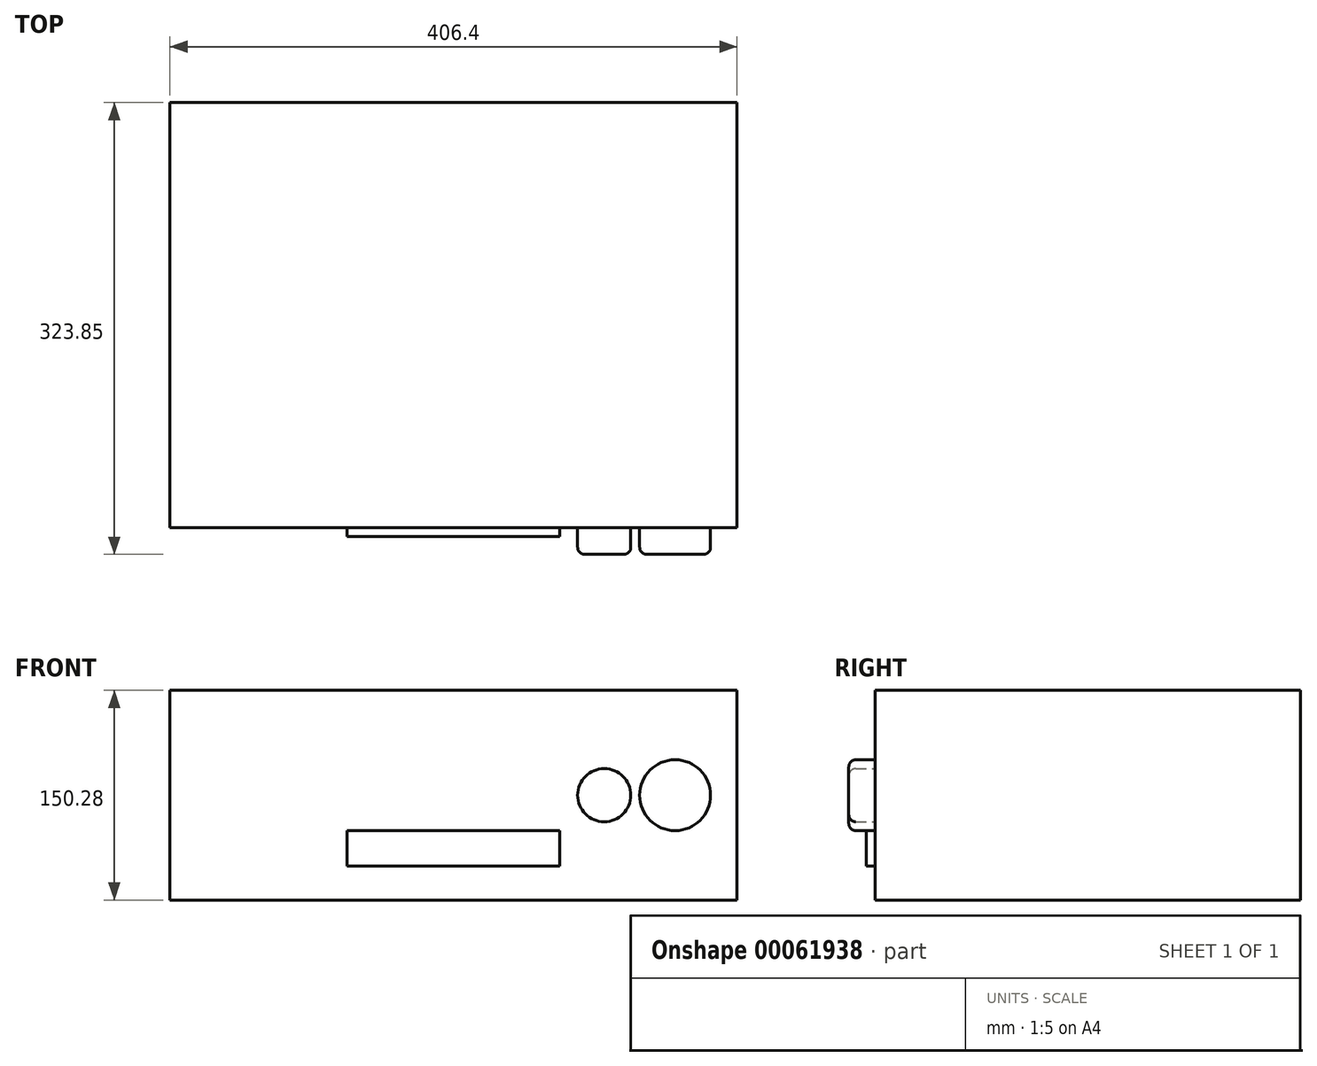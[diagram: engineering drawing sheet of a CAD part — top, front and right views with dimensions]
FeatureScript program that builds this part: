
annotation { "Feature Type Name" : "Feature", "Feature Type Description" : "" }
export const myFeature = defineFeature(function(context is Context, id is Id, definition is map)
    precondition{}
    {
        {
            var Q0;
            Q0=qCreatedBy(makeId("Front.planeOp"),FACE);
            var sketch = newSketch(context, id + "F0", { "sketchPlane" : qUnion([Q0])});
            skLineSegment(sketch, "E0.rect.bottom", {"start": v(203.2, -75.14) * mm, "end": v(-203.2, -75.14) * mm});
            skLineSegment(sketch, "E0.rect.top", {"start": v(203.2, 75.14) * mm, "end": v(-203.2, 75.14) * mm});
            skLineSegment(sketch, "E0.rect.left", {"start": v(203.2, -75.14) * mm, "end": v(203.2, 75.14) * mm});
            skLineSegment(sketch, "E0.rect.right", {"start": v(-203.2, -75.14) * mm, "end": v(-203.2, 75.14) * mm});
            skPoint(sketch, "E0.rect.middle", {"position": v(0, 0) * mm});
            skSolve(sketch);
        }
        {
            var Q0;
            Q0=makeQuery(id+"F0.imprint","IMPRINT",FACE,{"disambiguationData":[TD([[makeQuery(id+"F0.imprint","IMPRINT",EDGE,{"derivedFrom":sQuery(id+"F0.wireOp",EDGE,"E0.rect.bottom")}),-1.0]])]});
            extrude(context, id + "F1", {"entities" : qUnion([Q0]), "oppositeDirection" : true, "depth" : 304.8 * mm});
        }
        {
            var Q0;
            Q0=makeQuery(id+"F1.opExtrude","CAP_FACE",FACE,{"disambiguationData":[OSD([sQuery(id+"F0.wireOp",EDGE,"E0.rect.bottom"),sQuery(id+"F0.wireOp",EDGE,"E0.rect.top"),sQuery(id+"F0.wireOp",EDGE,"E0.rect.left"),sQuery(id+"F0.wireOp",EDGE,"E0.rect.right")])],"isStart":true});
            var sketch = newSketch(context, id + "F2", { "sketchPlane" : qUnion([Q0])});
            skLineSegment(sketch, "E1", {"start": v(203.2, 0) * mm, "end": v(158.75, 0) * mm, "construction": true});
            skPoint(sketch, "E1.endSnap0", {"position": v(203.2, 0) * mm});
            skLineSegment(sketch, "E2", {"start": v(158.75, 0) * mm, "end": v(107.95, 0) * mm, "construction": true});
            skCircle(sketch, "E3", {"center": v(158.75, 0) * mm, "radius": 25.4 * mm});
            skCircle(sketch, "E4", {"center": v(107.95, 0) * mm, "radius": 19.05 * mm});
            skSolve(sketch);
        }
        {
            var Q0;
            Q0=makeQuery(id+"F2.imprint","IMPRINT",FACE,{"disambiguationData":[TD([[makeQuery(id+"F2.imprint","IMPRINT",EDGE,{"derivedFrom":sQuery(id+"F2.wireOp",EDGE,"E4")}),1.0]])]});
            var Q1;
            Q1=makeQuery(id+"F2.imprint","IMPRINT",FACE,{"disambiguationData":[TD([[makeQuery(id+"F2.imprint","IMPRINT",EDGE,{"derivedFrom":sQuery(id+"F2.wireOp",EDGE,"E3")}),1.0]])]});
            extrude(context, id + "F3", {"entities" : qUnion([Q0, Q1]), "depth" : 19.05 * mm});
        }
        {
            var Q0;
            Q0=makeQuery(id+"F3.opExtrude","CAP_EDGE",EDGE,{"disambiguationData":[OSD([sQuery(id+"F2.wireOp",EDGE,"E4")])],"isStart":false});
            var Q1;
            Q1=makeQuery(id+"F3.opExtrude","CAP_EDGE",EDGE,{"disambiguationData":[OSD([sQuery(id+"F2.wireOp",EDGE,"E3")])],"isStart":false});
            fillet(context, id + "F4", {"entities" : qUnion([Q0, Q1]), "radius" : 5.08 * mm, "tangentPropagation" : true, "allowEdgeOverflow" : false});
        }
        {
            var Q0;
            Q0=makeQuery(id+"F1.opExtrude","CAP_FACE",FACE,{"disambiguationData":[OSD([sQuery(id+"F0.wireOp",EDGE,"E0.rect.bottom"),sQuery(id+"F0.wireOp",EDGE,"E0.rect.top"),sQuery(id+"F0.wireOp",EDGE,"E0.rect.left"),sQuery(id+"F0.wireOp",EDGE,"E0.rect.right")])],"isStart":true});
            var sketch = newSketch(context, id + "F5", { "sketchPlane" : qUnion([Q0])});
            skLineSegment(sketch, "E5.rect.bottom", {"start": v(-76.2, -12.7) * mm, "end": v(76.2, -12.7) * mm});
            skLineSegment(sketch, "E5.rect.top", {"start": v(-76.2, 12.7) * mm, "end": v(76.2, 12.7) * mm});
            skLineSegment(sketch, "E5.rect.left", {"start": v(-76.2, -12.7) * mm, "end": v(-76.2, 12.7) * mm});
            skLineSegment(sketch, "E5.rect.right", {"start": v(76.2, -12.7) * mm, "end": v(76.2, 12.7) * mm});
            skPoint(sketch, "E5.rect.middle", {"position": v(0, 0) * mm});
            skSolve(sketch);
        }
        {
            var Q0;
            Q0=makeQuery(id+"F5.imprint","IMPRINT",FACE,{"disambiguationData":[TD([[makeQuery(id+"F5.imprint","IMPRINT",EDGE,{"derivedFrom":sQuery(id+"F5.wireOp",EDGE,"E5.rect.bottom")}),1.0]])]});
            extrude(context, id + "F6", {"entities" : qUnion([Q0]), "depth" : 6.35 * mm});
        }
        {
            var Q0;
            Q0=makeQuery(id+"F6.opExtrude","SWEPT_BODY",BODY,{"disambiguationData":[OSD([sQuery(id+"F5.wireOp",EDGE,"E5.rect.bottom"),sQuery(id+"F5.wireOp",EDGE,"E5.rect.top"),sQuery(id+"F5.wireOp",EDGE,"E5.rect.left"),sQuery(id+"F5.wireOp",EDGE,"E5.rect.right")])]});
            transform(context, id + "F7", {"entities" : qUnion([Q0]), "transformType" : TransformType.TRANSLATION_3D, "dx" : 0 * mm, "dy" : 0 * mm, "dz" : -38.1 * mm, "makeCopy" : false});
        }
    });
